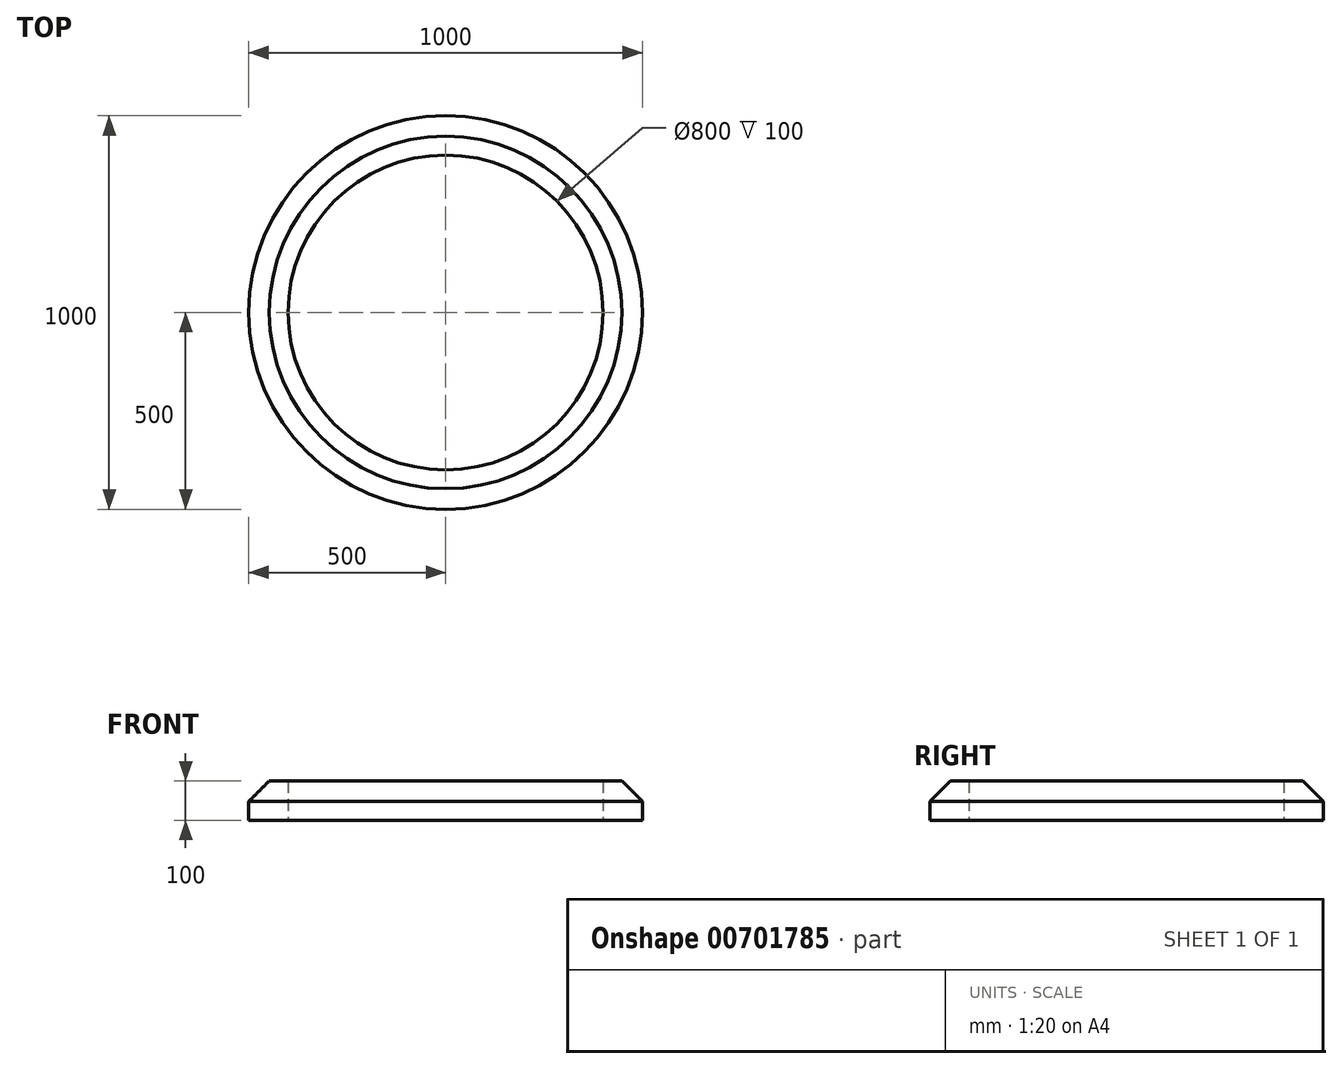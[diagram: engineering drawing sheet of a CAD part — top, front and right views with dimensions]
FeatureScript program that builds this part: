
annotation { "Feature Type Name" : "Feature", "Feature Type Description" : "" }
export const myFeature = defineFeature(function(context is Context, id is Id, definition is map)
    precondition{}
    {
        {
            var Q0;
            Q0=qCreatedBy(makeId("Top.planeOp"),FACE);
            var sketch = newSketch(context, id + "F0", { "sketchPlane" : qUnion([Q0])});
            skCircle(sketch, "E0", {"center": v(0, 0) * mm, "radius": 500 * mm});
            skCircle(sketch, "E1", {"center": v(0, 0) * mm, "radius": 400 * mm});
            skSolve(sketch);
        }
        {
            var Q0;
            Q0=makeQuery(id+"F0.imprint","IMPRINT",FACE,{"disambiguationData":[TD([[makeQuery(id+"F0.imprint","IMPRINT",EDGE,{"derivedFrom":sQuery(id+"F0.wireOp",EDGE,"E0")}),1.0]])]});
            extrude(context, id + "F1", {"entities" : qUnion([Q0]), "depth" : 100 * mm, "offsetDistance" : 25 * mm});
        }
        {
            var Q0;
            Q0=qCreatedBy(makeId("Front.planeOp"),FACE);
            var sketch = newSketch(context, id + "F2", { "sketchPlane" : qUnion([Q0])});
            skLineSegment(sketch, "E2", {"start": v(-447.74, 100) * mm, "end": v(-547.74, 0) * mm});
            skLineSegment(sketch, "E3", {"start": v(-547.74, 0) * mm, "end": v(-547.74, 100) * mm});
            skLineSegment(sketch, "E4", {"start": v(-547.74, 100) * mm, "end": v(-447.74, 100) * mm});
            skLineSegment(sketch, "E5", {"start": v(0, 0) * mm, "end": v(0, 234.07) * mm, "construction": true});
            skSolve(sketch);
        }
        {
            var Q0;
            Q0=makeQuery(id+"F2.imprint","IMPRINT",FACE,{"disambiguationData":[TD([[makeQuery(id+"F2.imprint","IMPRINT",EDGE,{"derivedFrom":sQuery(id+"F2.wireOp",EDGE,"E2")}),-1.0]])]});
            var Q1;
            Q1=sQuery(id+"F2.wireOp",EDGE,"E5");
            revolve(context, id + "F3", {"operationType" : NewBodyOperationType.REMOVE, "entities" : qUnion([Q0]), "axis" : qUnion([Q1]), "revolveType" : RevolveType.FULL, "oppositeDirection" : true});
        }
    });
